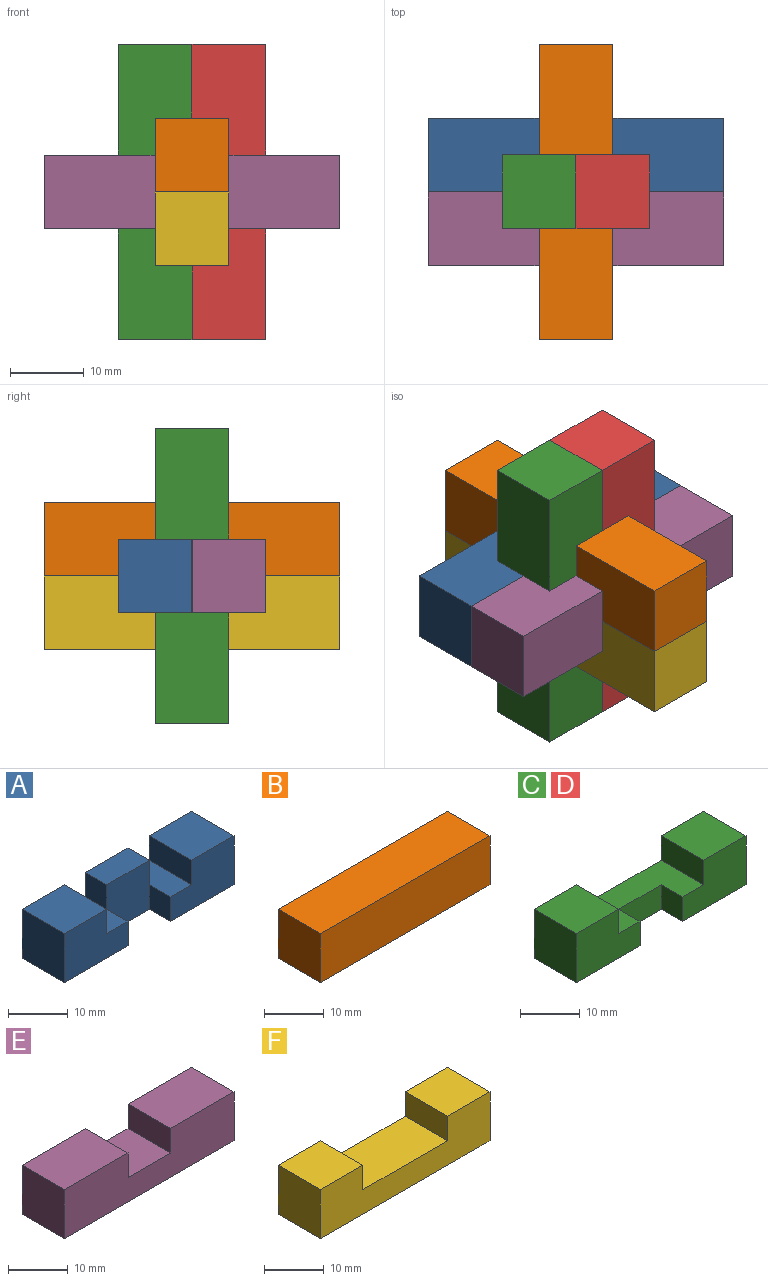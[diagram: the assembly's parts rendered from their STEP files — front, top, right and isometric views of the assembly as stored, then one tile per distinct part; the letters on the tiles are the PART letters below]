
ASSEMBLY  parts=6 mates=5
PART A: 18 faces, bbox 40x10x10 mm
  f0: plane 10x5mm, normal (0,0,1), area 50mm2, adj f1,f5,f11,f12,f16
  f1: plane 15x10mm, normal (0,-1,0), area 125mm2, adj f0,f2,f4,f7,f11,f12
  f2: plane 40x10mm, normal (0,0,-1), area 350mm2, adj f1,f3,f5,f6,f7,f12,f13,f14
  f3: plane 15x10mm, normal (0,-1,0), area 125mm2, adj f2,f6,f8,f9,f10,f13
  f4: plane 10x10mm, normal (0,0,1), area 100mm2, adj f1,f5,f7,f11
  f5: plane 40x10mm, normal (0,1,0), area 350mm2, adj f0,f2,f4,f6,f7,f8,f9,f10
  f6: plane 10x10mm, normal (-1,0,0), area 100mm2, adj f2,f3,f5,f8
  f7: plane 10x10mm, normal (1,0,0), area 100mm2, adj f1,f2,f4,f5
  f8: plane 10x10mm, normal (0,0,1), area 100mm2, adj f3,f5,f6,f9
  f9: plane 10x5mm, normal (1,0,0), area 50mm2, adj f3,f5,f8,f10
  f10: plane 10x5mm, normal (0,0,1), area 50mm2, adj f3,f5,f9,f13,f15
  f11: plane 10x5mm, normal (-1,0,0), area 50mm2, adj f0,f1,f4,f5
  f12: plane 5x5mm, normal (-1,0,0), area 25mm2, adj f0,f1,f2,f14
  f13: plane 5x5mm, normal (1,0,0), area 25mm2, adj f2,f3,f10,f14
  f14: plane 10x10mm, normal (0,-1,0), area 100mm2, adj f2,f12,f13,f15,f16,f17
  f15: plane 5x5mm, normal (-1,0,0), area 25mm2, adj f5,f10,f14,f17
  f16: plane 5x5mm, normal (1,0,0), area 25mm2, adj f0,f5,f14,f17
  f17: plane 10x5mm, normal (0,0,1), area 50mm2, adj f5,f14,f15,f16
PART B: 6 faces, bbox 40x10x10 mm
  f0: plane 40x10mm, normal (0,1,0), area 400mm2, adj f1,f3,f4,f5
  f1: plane 10x10mm, normal (-1,0,0), area 100mm2, adj f0,f2,f4,f5
  f2: plane 40x10mm, normal (0,-1,0), area 400mm2, adj f1,f3,f4,f5
  f3: plane 10x10mm, normal (1,0,0), area 100mm2, adj f0,f2,f4,f5
  f4: plane 40x10mm, normal (0,0,1), area 400mm2, adj f0,f1,f2,f3
  f5: plane 40x10mm, normal (0,0,-1), area 400mm2, adj f0,f1,f2,f3
PART C: 14 faces, bbox 40x10x10 mm
  f0: plane 15x10mm, normal (0,-1,0), area 125mm2, adj f1,f3,f6,f9,f10,f11
  f1: plane 40x10mm, normal (0,0,-1), area 350mm2, adj f0,f2,f4,f5,f6,f11,f12,f13
  f2: plane 15x10mm, normal (0,-1,0), area 125mm2, adj f1,f5,f7,f8,f9,f12
  f3: plane 10x10mm, normal (0,0,1), area 100mm2, adj f0,f4,f6,f10
  f4: plane 40x10mm, normal (0,1,0), area 300mm2, adj f1,f3,f5,f6,f7,f8,f9,f10
  f5: plane 10x10mm, normal (-1,0,0), area 100mm2, adj f1,f2,f4,f7
  f6: plane 10x10mm, normal (1,0,0), area 100mm2, adj f0,f1,f3,f4
  f7: plane 10x10mm, normal (0,0,1), area 100mm2, adj f2,f4,f5,f8
  f8: plane 10x5mm, normal (1,0,0), area 50mm2, adj f2,f4,f7,f9
  f9: plane 20x10mm, normal (0,0,1), area 150mm2, adj f0,f2,f4,f8,f10,f11,f12,f13
  f10: plane 10x5mm, normal (-1,0,0), area 50mm2, adj f0,f3,f4,f9
  f11: plane 5x5mm, normal (-1,0,0), area 25mm2, adj f0,f1,f9,f13
  f12: plane 5x5mm, normal (1,0,0), area 25mm2, adj f1,f2,f9,f13
  f13: plane 10x5mm, normal (0,-1,0), area 50mm2, adj f1,f9,f11,f12
PART D: same geometry as C
PART E: 10 faces, bbox 40x10x10 mm
  f0: plane 40x10mm, normal (0,-1,0), area 350mm2, adj f1,f3,f4,f5,f6,f7,f8,f9
  f1: plane 15x10mm, normal (0,0,1), area 150mm2, adj f0,f2,f4,f9
  f2: plane 40x10mm, normal (0,1,0), area 350mm2, adj f1,f3,f4,f5,f6,f7,f8,f9
  f3: plane 10x10mm, normal (-1,0,0), area 100mm2, adj f0,f2,f5,f6
  f4: plane 10x10mm, normal (1,0,0), area 100mm2, adj f0,f1,f2,f6
  f5: plane 15x10mm, normal (0,0,1), area 150mm2, adj f0,f2,f3,f7
  f6: plane 40x10mm, normal (0,0,-1), area 400mm2, adj f0,f2,f3,f4
  f7: plane 10x5mm, normal (1,0,0), area 50mm2, adj f0,f2,f5,f8
  f8: plane 10x10mm, normal (0,0,1), area 100mm2, adj f0,f2,f7,f9
  f9: plane 10x5mm, normal (-1,0,0), area 50mm2, adj f0,f1,f2,f8
PART F: 10 faces, bbox 40x10x10 mm
  f0: plane 40x10mm, normal (0,-1,0), area 300mm2, adj f1,f3,f4,f5,f6,f7,f8,f9
  f1: plane 10x10mm, normal (0,0,1), area 100mm2, adj f0,f2,f4,f9
  f2: plane 40x10mm, normal (0,1,0), area 300mm2, adj f1,f3,f4,f5,f6,f7,f8,f9
  f3: plane 10x10mm, normal (-1,0,0), area 100mm2, adj f0,f2,f5,f6
  f4: plane 10x10mm, normal (1,0,0), area 100mm2, adj f0,f1,f2,f6
  f5: plane 10x10mm, normal (0,0,1), area 100mm2, adj f0,f2,f3,f7
  f6: plane 40x10mm, normal (0,0,-1), area 400mm2, adj f0,f2,f3,f4
  f7: plane 10x5mm, normal (1,0,0), area 50mm2, adj f0,f2,f5,f8
  f8: plane 20x10mm, normal (0,0,1), area 200mm2, adj f0,f2,f7,f9
  f9: plane 10x5mm, normal (-1,0,0), area 50mm2, adj f0,f1,f2,f8
PLACE A rot(axis=(0,0.71,-0.71),180deg) t=(-5,30,-10)mm
PLACE B rot(axis=(0.71,-0.71,0),180deg) t=(-5,20,0)mm
PLACE C rot(axis=(0,1,0),90deg) t=(-15,20,-10)mm
PLACE D rot(axis=(0,-1,0),90deg) t=(5,20,-10)mm
PLACE E rot(axis=(0,0,1),180deg) t=(-5,15,-15)mm
PLACE F rot(axis=(0,0,1),90deg) t=(-5,20,-20)mm
MATE fastened C.f7 <-> D.f3  axis (1,0,0) through (-5,20,5)mm
MATE fastened A.f14 <-> B.f4  axis (0,0,1) through (0,20,-10)mm
MATE fastened E.f2 <-> F.f7  axis (0,-1,0) through (0,10,-10)mm
MATE fastened F.f3 <-> B.f3  axis (0,-1,0) through (0,0,-10)mm
MATE fastened D.f1 <-> A.f9  axis (1,0,0) through (5,20,-5)mm
